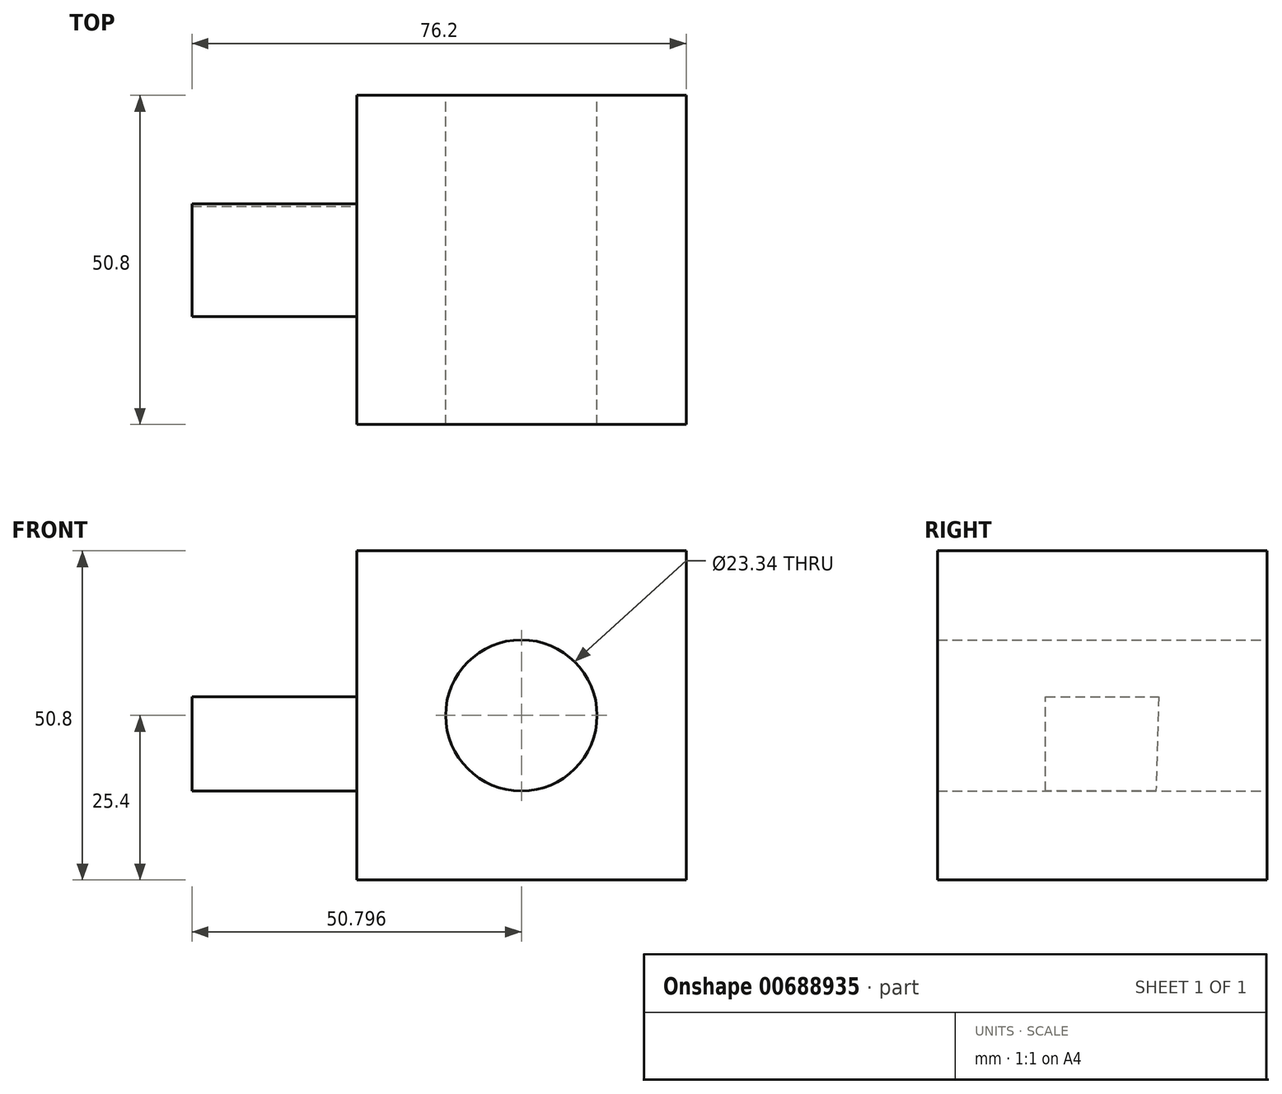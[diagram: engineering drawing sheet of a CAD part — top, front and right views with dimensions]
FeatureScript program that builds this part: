
annotation { "Feature Type Name" : "Feature", "Feature Type Description" : "" }
export const myFeature = defineFeature(function(context is Context, id is Id, definition is map)
    precondition{}
    {
        {
            var Q0;
            Q0=qCreatedBy(makeId("Front.planeOp"),FACE);
            var sketch = newSketch(context, id + "F0", { "sketchPlane" : qUnion([Q0])});
            skLineSegment(sketch, "E0", {"start": v(-62.4, 50.8) * mm, "end": v(-62.4, 0) * mm});
            skLineSegment(sketch, "E1", {"start": v(-62.4, 0) * mm, "end": v(-11.6, 0) * mm});
            skLineSegment(sketch, "E2", {"start": v(-11.6, 0) * mm, "end": v(-11.6, 50.8) * mm});
            skLineSegment(sketch, "E3", {"start": v(-11.6, 50.8) * mm, "end": v(-62.4, 50.8) * mm});
            skCircle(sketch, "E4", {"center": v(-37, 25.4) * mm, "radius": 11.67 * mm});
            skLineSegment(sketch, "E5", {"start": v(-37, 25.4) * mm, "end": v(-37, 50.8) * mm});
            skLineSegment(sketch, "E6", {"start": v(-37, 25.4) * mm, "end": v(-11.6, 25.4) * mm});
            skLineSegment(sketch, "E7", {"start": v(-37, 25.4) * mm, "end": v(-37, 0) * mm});
            skLineSegment(sketch, "E8", {"start": v(-37, 0) * mm, "end": v(-37, 25.4) * mm});
            skLineSegment(sketch, "E9", {"start": v(-37, 25.4) * mm, "end": v(-62.4, 25.4) * mm});
            skSolve(sketch);
        }
        {
            var Q0;
            Q0 = qSketchRegion(id + "F0", true);
            var Q1;
            Q1 = qSketchRegion(id + "FCn0cohklNKEflF_0", true);
            var Q2;
            Q2 = qSketchRegion(id + "FlMuxpCFa37PSCN_0", true);
            var Q3;
            Q3 = qSketchRegion(id + "F6WA9BDRIpn8ZUE_0", true);
            extrude(context, id + "F1", {"entities" : qUnion([Q0, Q1, Q2, Q3]), "depth" : 50.8 * mm, "offsetDistance" : 25.4 * mm});
        }
        {
            var Q0;
            Q0=makeQuery(id+"F1.opExtrude","SWEPT_FACE",FACE,{"disambiguationData":[OSD([sQuery(id+"F0.wireOp",EDGE,"E0")])]});
            var sketch = newSketch(context, id + "F2", { "sketchPlane" : qUnion([Q0])});
            skLineSegment(sketch, "E10", {"start": v(17.14, 13.72) * mm, "end": v(34.16, 13.72) * mm});
            skLineSegment(sketch, "E11", {"start": v(34.16, 13.72) * mm, "end": v(34.16, 28.3) * mm});
            skLineSegment(sketch, "E12", {"start": v(34.16, 28.3) * mm, "end": v(16.74, 28.3) * mm});
            skLineSegment(sketch, "E13", {"start": v(16.74, 28.3) * mm, "end": v(17.14, 13.72) * mm});
            skSolve(sketch);
        }
        {
            var Q0;
            Q0=makeQuery(id+"F2.imprint","IMPRINT",FACE,{"disambiguationData":[TD([[makeQuery(id+"F2.imprint","IMPRINT",EDGE,{"derivedFrom":sQuery(id+"F2.wireOp",EDGE,"E10")}),1.0]])]});
            extrude(context, id + "F3", {"entities" : qUnion([Q0]), "operationType" : NewBodyOperationType.ADD, "depth" : 25.4 * mm, "offsetDistance" : 25.4 * mm});
        }
    });
